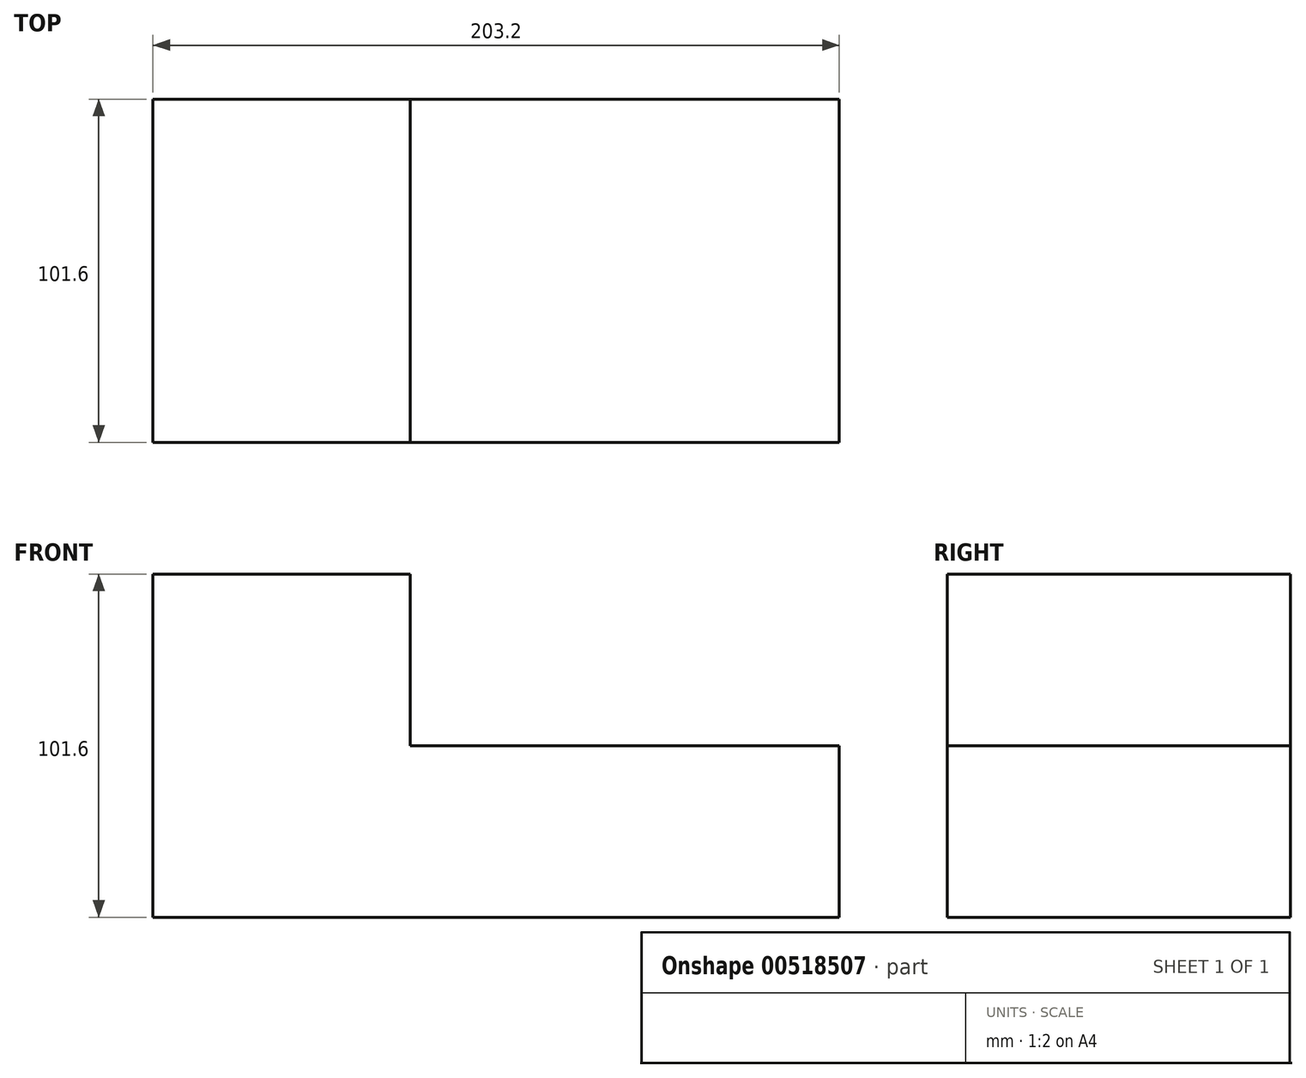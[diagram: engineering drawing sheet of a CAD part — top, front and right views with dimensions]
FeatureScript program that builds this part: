
annotation { "Feature Type Name" : "Feature", "Feature Type Description" : "" }
export const myFeature = defineFeature(function(context is Context, id is Id, definition is map)
    precondition{}
    {
        {
            var Q0;
            Q0=qCreatedBy(makeId("Front.planeOp"),FACE);
            var sketch = newSketch(context, id + "F0", { "sketchPlane" : qUnion([Q0])});
            skLineSegment(sketch, "E0.bottom", {"start": v(-122.85, 0) * mm, "end": v(80.35, 0) * mm});
            skLineSegment(sketch, "E0.top", {"start": v(-122.85, 101.6) * mm, "end": v(-46.65, 101.6) * mm});
            skLineSegment(sketch, "E0.left", {"start": v(-122.85, 0) * mm, "end": v(-122.85, 101.6) * mm});
            skLineSegment(sketch, "E0.right", {"start": v(80.35, 0) * mm, "end": v(80.35, 50.8) * mm});
            skLineSegment(sketch, "E1.top", {"start": v(80.35, 50.8) * mm, "end": v(-46.65, 50.8) * mm});
            skLineSegment(sketch, "E1.right", {"start": v(-46.65, 101.6) * mm, "end": v(-46.65, 50.8) * mm});
            skSolve(sketch);
        }
        {
            var Q0;
            Q0=makeQuery(id+"F0.imprint","IMPRINT",FACE,{"disambiguationData":[TD([[makeQuery(id+"F0.imprint","IMPRINT",EDGE,{"derivedFrom":sQuery(id+"F0.wireOp",EDGE,"E0.bottom")}),1.0]])]});
            extrude(context, id + "F1", {"entities" : qUnion([Q0]), "depth" : 101.6 * mm});
        }
    });
